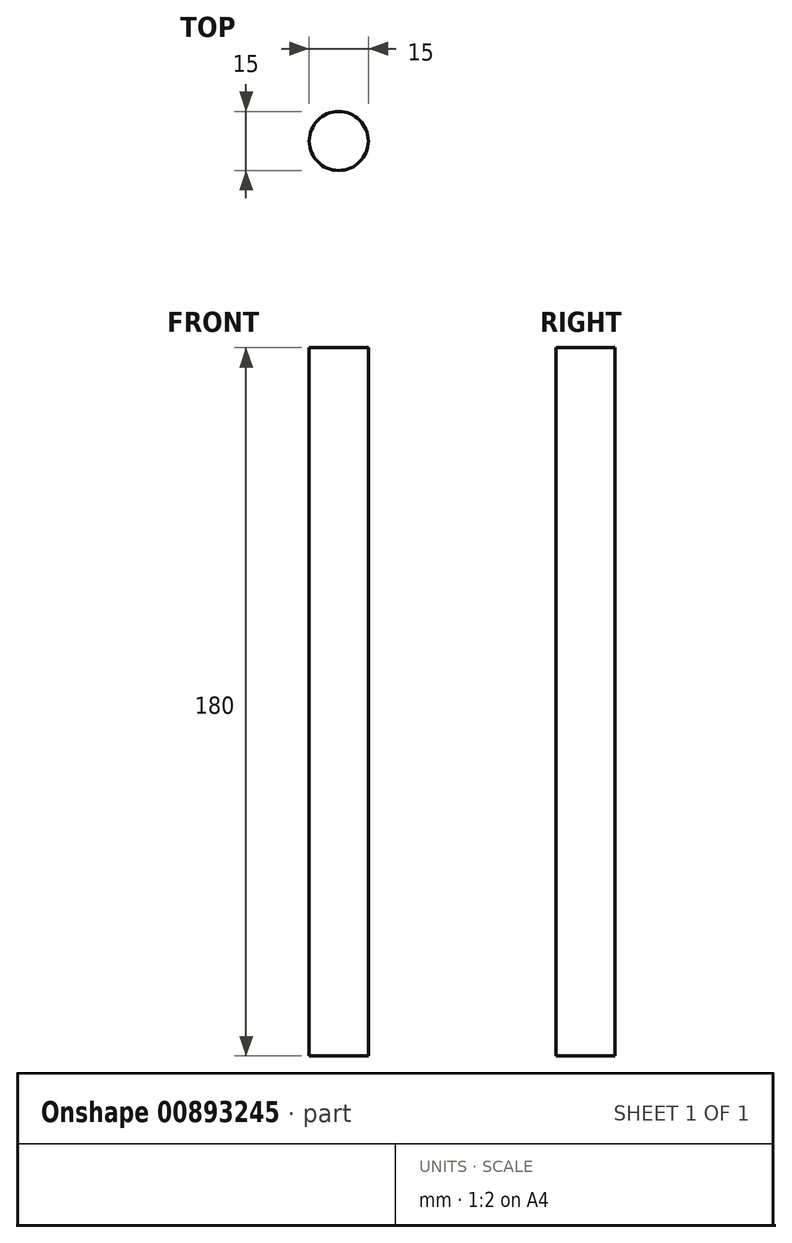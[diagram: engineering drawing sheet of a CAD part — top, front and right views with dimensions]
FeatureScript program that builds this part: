
annotation { "Feature Type Name" : "Feature", "Feature Type Description" : "" }
export const myFeature = defineFeature(function(context is Context, id is Id, definition is map)
    precondition{}
    {
        {
            var Q0;
            Q0=qCreatedBy(makeId("Top.planeOp"),FACE);
            var sketch = newSketch(context, id + "F0", { "sketchPlane" : qUnion([Q0])});
            skCircle(sketch, "E0", {"center": v(0, 0) * mm, "radius": 7.5 * mm});
            skSolve(sketch);
        }
        {
            var Q0;
            Q0=makeQuery(id+"F0.imprint","IMPRINT",FACE,{"disambiguationData":[TD([[makeQuery(id+"F0.imprint","IMPRINT",EDGE,{"derivedFrom":sQuery(id+"F0.wireOp",EDGE,"E0")}),1.0]])]});
            extrude(context, id + "F1", {"entities" : qUnion([Q0]), "depth" : 180 * mm, "offsetDistance" : 25 * mm});
        }
    });
